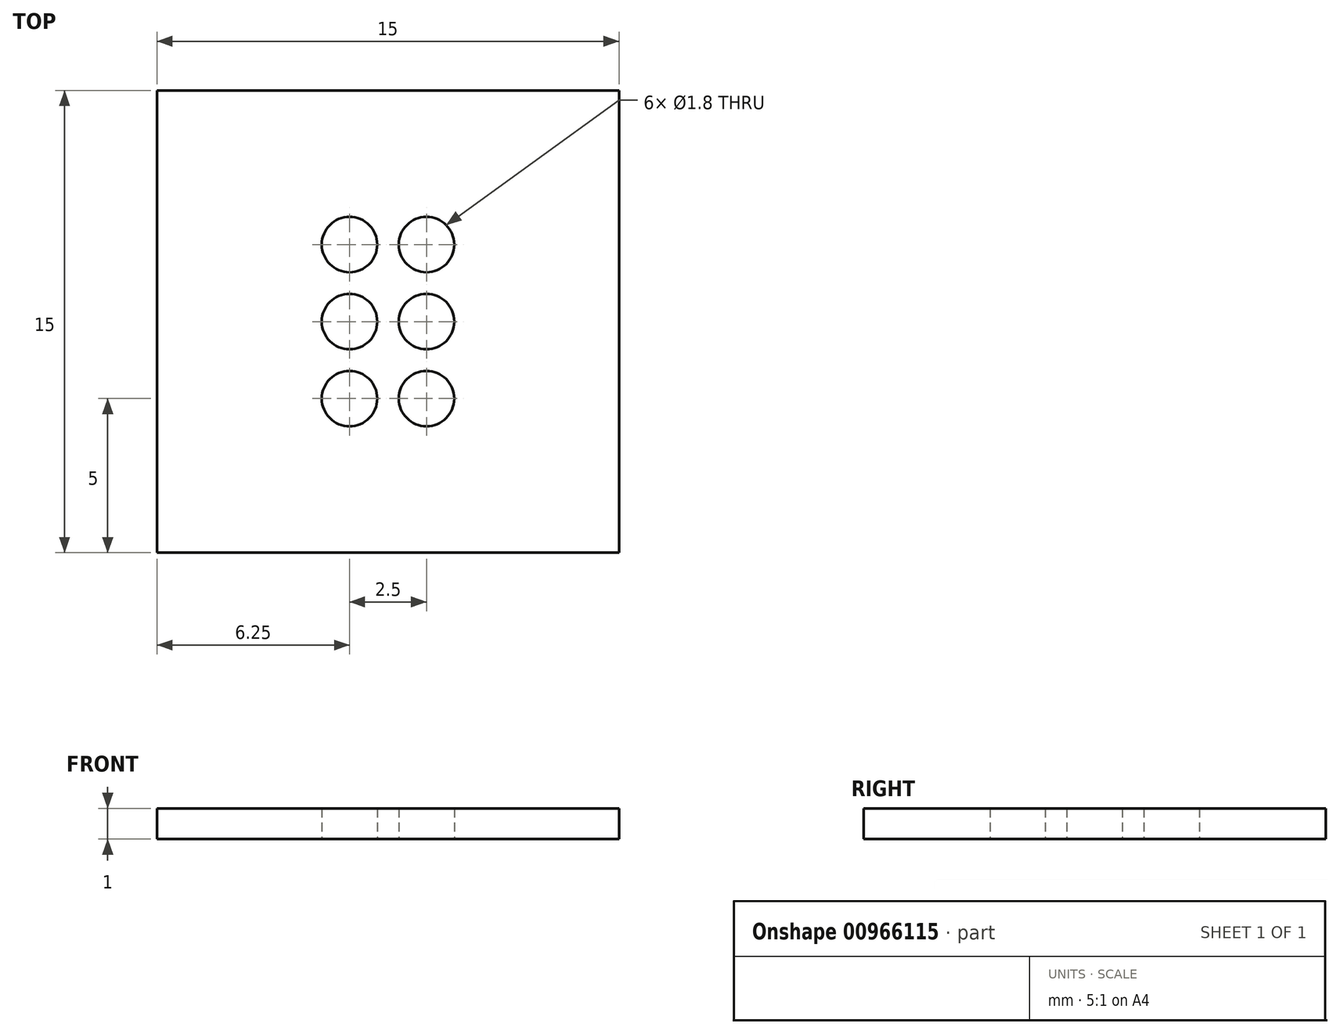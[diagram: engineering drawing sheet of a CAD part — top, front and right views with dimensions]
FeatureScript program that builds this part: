
annotation { "Feature Type Name" : "Feature", "Feature Type Description" : "" }
export const myFeature = defineFeature(function(context is Context, id is Id, definition is map)
    precondition{}
    {
        {
            var Q0;
            Q0=qCreatedBy(makeId("Top.planeOp"),FACE);
            var sketch = newSketch(context, id + "F0", { "sketchPlane" : qUnion([Q0])});
            skLineSegment(sketch, "E0.bottom", {"start": v(7.5, -7.5) * mm, "end": v(-7.5, -7.5) * mm});
            skLineSegment(sketch, "E0.top", {"start": v(7.5, 7.5) * mm, "end": v(-7.5, 7.5) * mm});
            skLineSegment(sketch, "E0.left", {"start": v(7.5, -7.5) * mm, "end": v(7.5, 7.5) * mm});
            skLineSegment(sketch, "E0.right", {"start": v(-7.5, -7.5) * mm, "end": v(-7.5, 7.5) * mm});
            skPoint(sketch, "E0.middle", {"position": v(0, 0) * mm});
            skCircle(sketch, "E1", {"center": v(-1.25, 0) * mm, "radius": 0.9 * mm});
            skCircle(sketch, "E2", {"center": v(-1.25, 2.5) * mm, "radius": 0.9 * mm});
            skCircle(sketch, "E3", {"center": v(-1.25, -2.5) * mm, "radius": 0.9 * mm});
            skCircle(sketch, "E4.MirrorC", {"center": v(1.25, 2.5) * mm, "radius": 0.9 * mm});
            skCircle(sketch, "E5.MirrorC", {"center": v(1.25, 0) * mm, "radius": 0.9 * mm});
            skCircle(sketch, "E6.MirrorC", {"center": v(1.25, -2.5) * mm, "radius": 0.9 * mm});
            skSolve(sketch);
        }
        {
            var Q0;
            Q0=makeQuery(id+"F0.imprint","IMPRINT",FACE,{"disambiguationData":[TD([[makeQuery(id+"F0.imprint","IMPRINT",EDGE,{"derivedFrom":sQuery(id+"F0.wireOp",EDGE,"E0.bottom")}),-1.0]])]});
            extrude(context, id + "F1", {"entities" : qUnion([Q0]), "depth" : 1 * mm, "offsetDistance" : 25 * mm});
        }
    });
